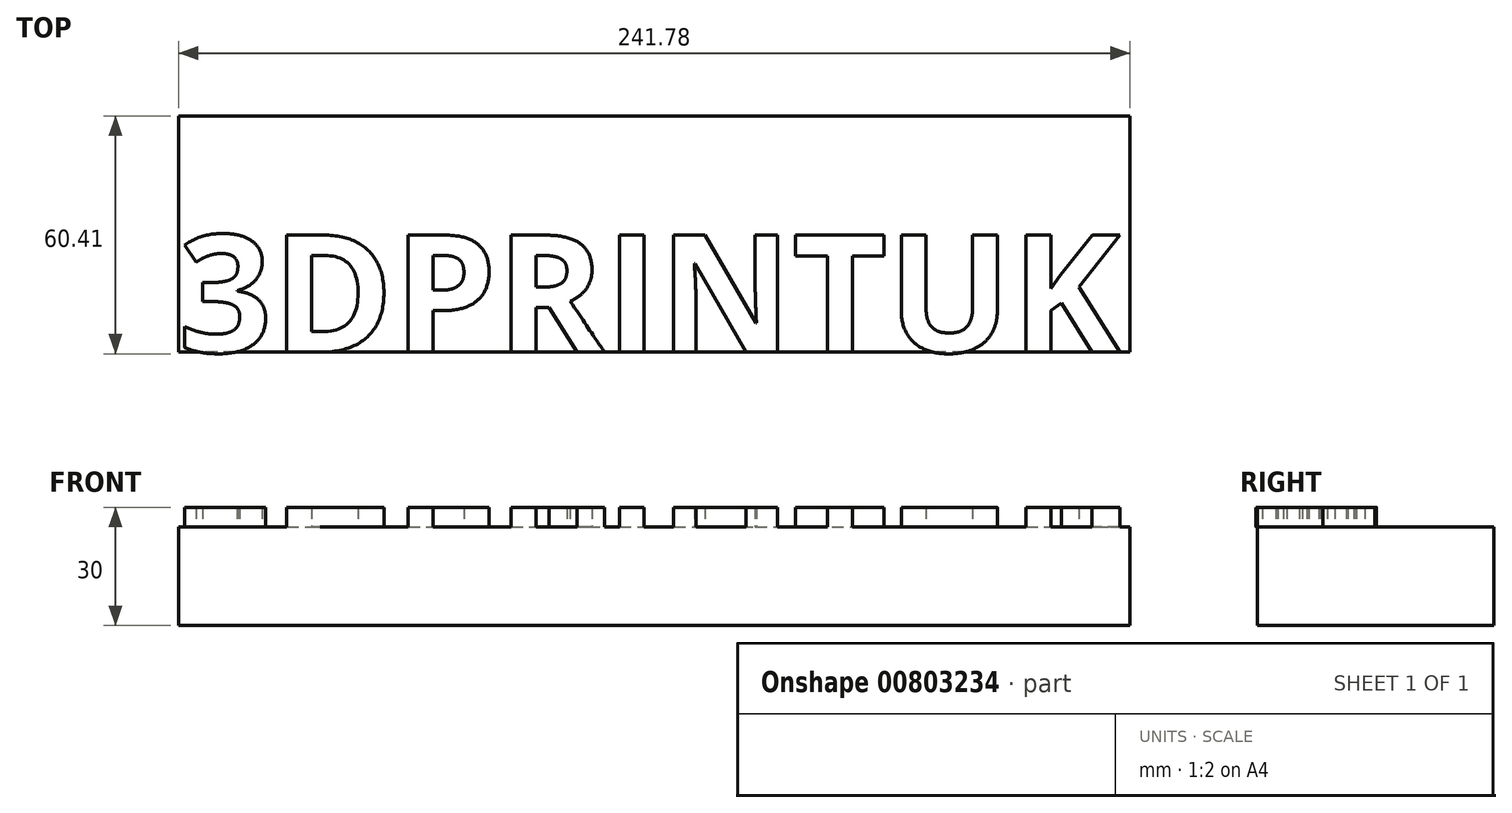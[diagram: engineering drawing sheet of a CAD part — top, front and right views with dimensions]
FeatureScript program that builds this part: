
annotation { "Feature Type Name" : "Feature", "Feature Type Description" : "" }
export const myFeature = defineFeature(function(context is Context, id is Id, definition is map)
    precondition{}
    {
        {
            var Q0;
            Q0=qCreatedBy(makeId("Top.planeOp"),FACE);
            var sketch = newSketch(context, id + "F0", { "sketchPlane" : qUnion([Q0])});
            skLineSegment(sketch, "E0.bottom", {"start": v(28.39, -30) * mm, "end": v(-28.39, -30) * mm});
            skLineSegment(sketch, "E0.top", {"start": v(28.39, 30) * mm, "end": v(-28.39, 30) * mm});
            skLineSegment(sketch, "E0.left", {"start": v(28.39, -30) * mm, "end": v(28.39, 30) * mm});
            skLineSegment(sketch, "E0.right", {"start": v(-28.39, -30) * mm, "end": v(-28.39, 30) * mm});
            skPoint(sketch, "E0.middle", {"position": v(0, 0) * mm});
            skSolve(sketch);
        }
        {
            var Q0;
            Q0 = qSketchRegion(id + "F0", true);
            extrude(context, id + "F1", {"entities" : qUnion([Q0]), "depth" : 25 * mm, "offsetDistance" : 25 * mm});
        }
        {
            var Q0;
            Q0=makeQuery(id+"F1.opExtrude","CAP_FACE",FACE,{"disambiguationData":[OSD([sQuery(id+"F0.wireOp",EDGE,"E0.bottom"),sQuery(id+"F0.wireOp",EDGE,"E0.top"),sQuery(id+"F0.wireOp",EDGE,"E0.left"),sQuery(id+"F0.wireOp",EDGE,"E0.right")])],"isStart":false});
            var sketch = newSketch(context, id + "F2", { "sketchPlane" : qUnion([Q0])});
            skText(sketch, "E1", { "text": "3DPRINTUK", "fontName": "OpenSans-Bold.ttf"});
            const initialGuessF2  = {"E1": [-0.02839, -0.03, 1, 0, 0.03]};
            skSetInitialGuess(sketch, initialGuessF2);
            skSolve(sketch);
        }
        {
            var Q0;
            Q0=makeQuery(id+"F1.opExtrude","SWEPT_FACE",FACE,{"disambiguationData":[OSD([sQuery(id+"F0.wireOp",EDGE,"E0.left")])]});
            extrude(context, id + "F3", {"entities" : qUnion([Q0]), "operationType" : NewBodyOperationType.ADD, "depth" : 185 * mm, "offsetDistance" : 25 * mm});
        }
        {
            var Q0;
            Q0 = qSketchRegion(id + "F2", true);
            extrude(context, id + "F4", {"entities" : qUnion([Q0]), "operationType" : NewBodyOperationType.ADD, "depth" : 5 * mm, "offsetDistance" : 25 * mm});
        }
    });
